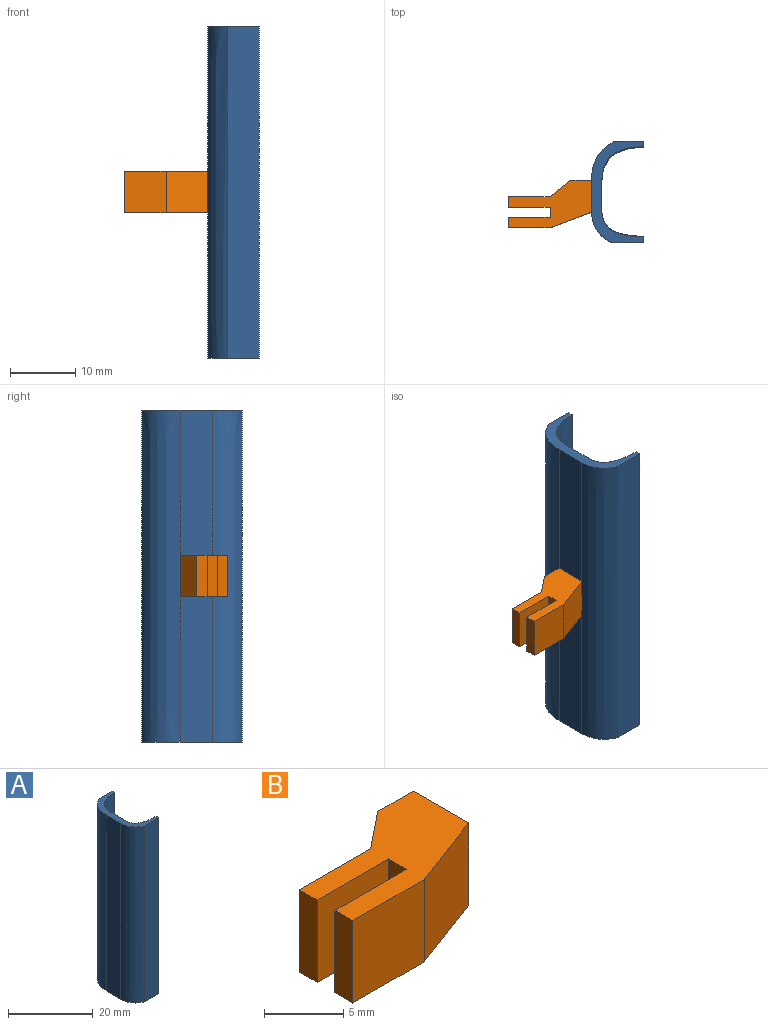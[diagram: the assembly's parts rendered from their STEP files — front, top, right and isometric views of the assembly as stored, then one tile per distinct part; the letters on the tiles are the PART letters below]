
ASSEMBLY  parts=2 mates=1
PART A: 12 faces, bbox 7.9x15.4x50.8 mm
  f0: plane 50.8x4.82mm, normal (0,-1,0), area 245mm2, adj f1,f9,f10,f11
  f1: plane 50.8x0.79mm, normal (1,0,0), area 40.3mm2, adj f0,f2,f10,f11
  f2: extruded ~50.8x6.35mm, area 424.1mm2, adj f1,f3,f10,f11
  f3: plane 50.8x4.92mm, normal (1,0,0), area 250mm2, adj f2,f4,f10,f11
  f4: extruded ~50.8x6.35mm, area 472.4mm2, adj f3,f5,f10,f11
  f5: plane 50.8x0.79mm, normal (1,0,0), area 40.3mm2, adj f4,f6,f10,f11
  f6: plane 50.8x4.39mm, normal (0,1,0), area 223mm2, adj f5,f7,f10,f11
  f7: extruded ~50.8x5.87mm, area 370.8mm2, adj f6,f8,f10,f11
  f8: plane 50.8x4.92mm, normal (-1,0,0), area 250mm2, adj f7,f9,f10,f11
  f9: extruded ~50.8x4.6mm, area 300.7mm2, adj f0,f8,f10,f11
  f10: plane 15.4x7.94mm, normal (0,0,1), area 34.6mm2, adj f0,f1,f2,f3,f4,f5,f6,f7
  f11: plane 15.4x7.94mm, normal (0,0,-1), area 34.6mm2, adj f0,f1,f2,f3,f4,f5,f6,f7
PART B: 13 faces, bbox 12.7x7.3x6.4 mm
  f0: plane 6.35x6.35mm, normal (0,1,0), area 40.3mm2, adj f1,f10,f11,f12
  f1: plane 6.35x1.59mm, normal (-1,0,0), area 10.1mm2, adj f0,f2,f11,f12
  f2: plane 6.35x6.35mm, normal (0,-1,0), area 40.3mm2, adj f1,f3,f11,f12
  f3: plane 6.35x6.35mm, normal (0.35,-0.94,0), area 43.1mm2, adj f2,f4,f11,f12
  f4: plane 6.35x4.92mm, normal (1,0,0), area 31.2mm2, adj f3,f5,f11,f12
  f5: plane 6.35x3.18mm, normal (0,1,0), area 20.2mm2, adj f4,f6,f11,f12
  f6: plane 6.35x3.18mm, normal (-0.62,0.78,0), area 25.8mm2, adj f5,f7,f11,f12
  f7: plane 6.35x6.35mm, normal (0,1,0), area 40.3mm2, adj f6,f8,f11,f12
  f8: plane 6.35x1.59mm, normal (-1,0,0), area 10.1mm2, adj f7,f9,f11,f12
  f9: plane 6.35x6.35mm, normal (0,-1,0), area 40.3mm2, adj f8,f10,f11,f12
  f10: plane 6.35x1.59mm, normal (-1,0,0), area 10.1mm2, adj f0,f9,f11,f12
  f11: plane 12.7x7.3mm, normal (0,0,1), area 54.9mm2, adj f0,f1,f2,f3,f4,f5,f6,f7
  f12: plane 12.7x7.3mm, normal (0,0,-1), area 54.9mm2, adj f0,f1,f2,f3,f4,f5,f6,f7
PLACE A t=(-23.21,3.1,-8.19)mm
PLACE B t=(-15.71,0.72,14.03)mm
MATE fastened B.f4 <-> A.f8  axis (1,0,0) through (-3.01,5.56,17.21)mm
